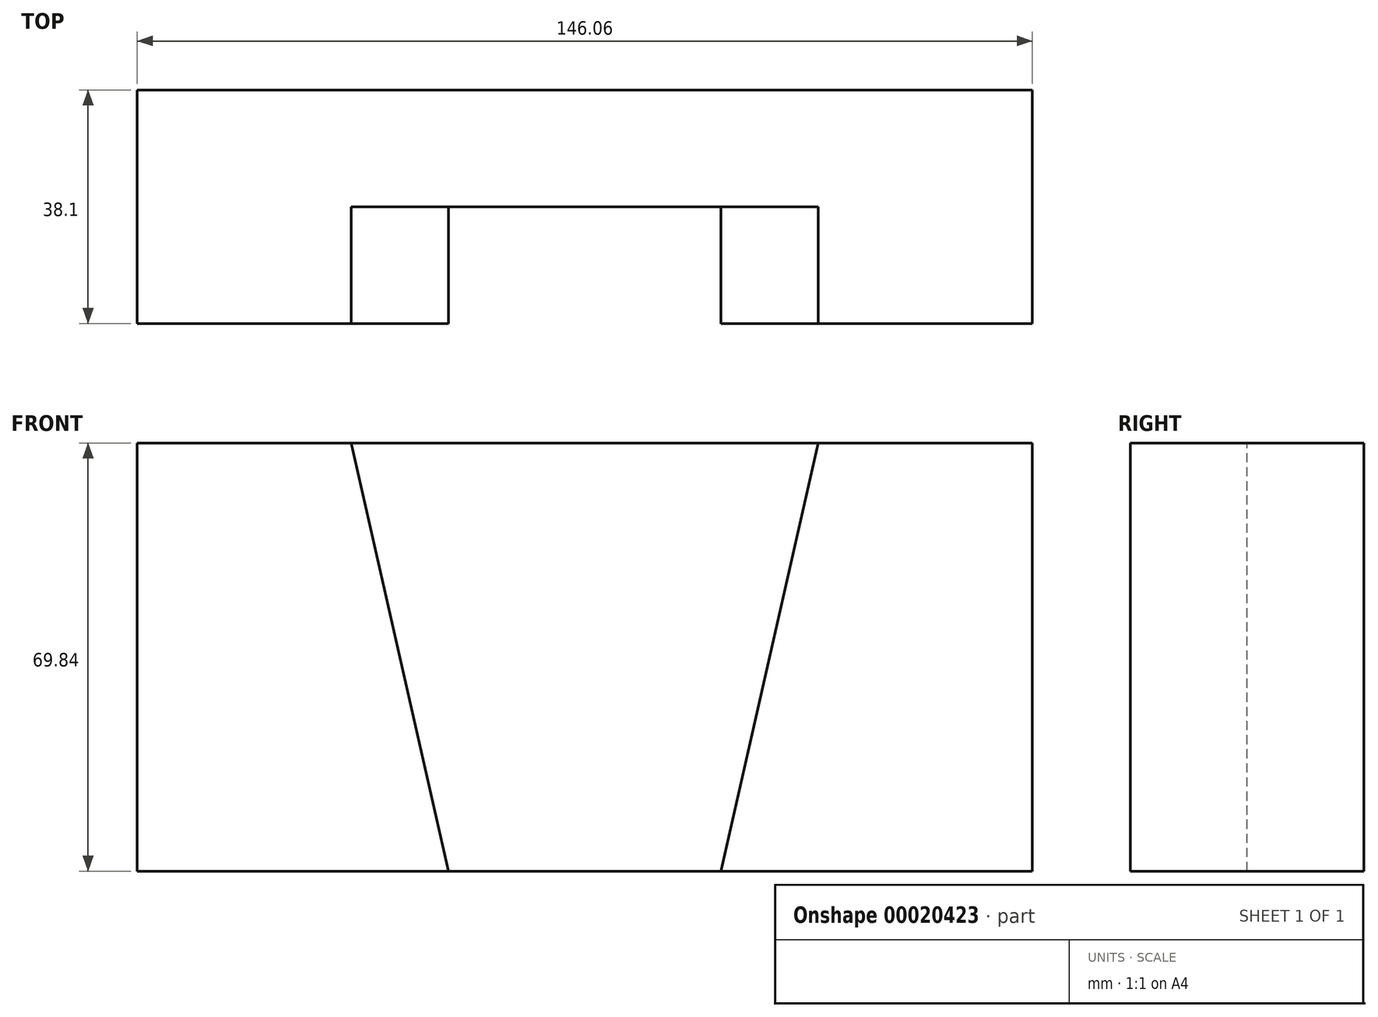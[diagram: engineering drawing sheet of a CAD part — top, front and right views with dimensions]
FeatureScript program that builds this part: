
annotation { "Feature Type Name" : "Feature", "Feature Type Description" : "" }
export const myFeature = defineFeature(function(context is Context, id is Id, definition is map)
    precondition{}
    {
        {
            var Q0;
            Q0=qCreatedBy(makeId("Front.planeOp"),FACE);
            var sketch = newSketch(context, id + "F0", { "sketchPlane" : qUnion([Q0])});
            skLineSegment(sketch, "E0.rect.bottom", {"start": v(73.03, -34.93) * mm, "end": v(-73.03, -34.93) * mm});
            skLineSegment(sketch, "E0.rect.top", {"start": v(73.02, 34.93) * mm, "end": v(-73.03, 34.93) * mm});
            skLineSegment(sketch, "E0.rect.left", {"start": v(73.03, -34.93) * mm, "end": v(73.03, 34.93) * mm});
            skLineSegment(sketch, "E0.rect.right", {"start": v(-73.02, -34.93) * mm, "end": v(-73.03, 34.92) * mm});
            skPoint(sketch, "E0.rect.middle", {"position": v(0, 0) * mm});
            skSolve(sketch);
        }
        {
            var Q0;
            Q0=makeQuery(id+"F0.imprint","IMPRINT",FACE,{"disambiguationData":[TD([[makeQuery(id+"F0.imprint","IMPRINT",EDGE,{"derivedFrom":sQuery(id+"F0.wireOp",EDGE,"E0.rect.bottom")}),-1.0]])]});
            extrude(context, id + "F1", {"entities" : qUnion([Q0]), "depth" : 19.05 * mm});
        }
        {
            var Q0;
            Q0=makeQuery(id+"F1.opExtrude","CAP_FACE",FACE,{"disambiguationData":[OSD([sQuery(id+"F0.wireOp",EDGE,"E0.rect.bottom"),sQuery(id+"F0.wireOp",EDGE,"E0.rect.top"),sQuery(id+"F0.wireOp",EDGE,"E0.rect.left"),sQuery(id+"F0.wireOp",EDGE,"E0.rect.right")])],"isStart":false});
            var sketch = newSketch(context, id + "F2", { "sketchPlane" : qUnion([Q0])});
            skLineSegment(sketch, "E1", {"start": v(-22.22, -34.93) * mm, "end": v(22.23, -34.93) * mm});
            skLineSegment(sketch, "E2", {"start": v(-38.1, 34.93) * mm, "end": v(38.1, 34.93) * mm});
            skLineSegment(sketch, "E3", {"start": v(-22.22, -34.93) * mm, "end": v(-38.1, 34.93) * mm});
            skLineSegment(sketch, "E4", {"start": v(22.23, -34.93) * mm, "end": v(38.1, 34.93) * mm});
            skSolve(sketch);
        }
        {
            var Q0;
            {var subQ1=sQuery(id+"F2.wireOp",EDGE,"E4");Q0=makeQuery(id+"F2.imprint","IMPRINT",FACE,{"disambiguationData":[TD([[makeQuery(id+"F2.imprint","IMPRINT",EDGE,{"derivedFrom":subQ1}),-1.0]])]});}
            var Q1;
            {var subQ1=sQuery(id+"F2.wireOp",EDGE,"E3");Q1=makeQuery(id+"F2.imprint","IMPRINT",FACE,{"disambiguationData":[TD([[makeQuery(id+"F2.imprint","IMPRINT",EDGE,{"derivedFrom":subQ1}),1.0]])]});}
            extrude(context, id + "F3", {"entities" : qUnion([Q0, Q1]), "operationType" : NewBodyOperationType.ADD, "depth" : 19.05 * mm});
        }
    });
